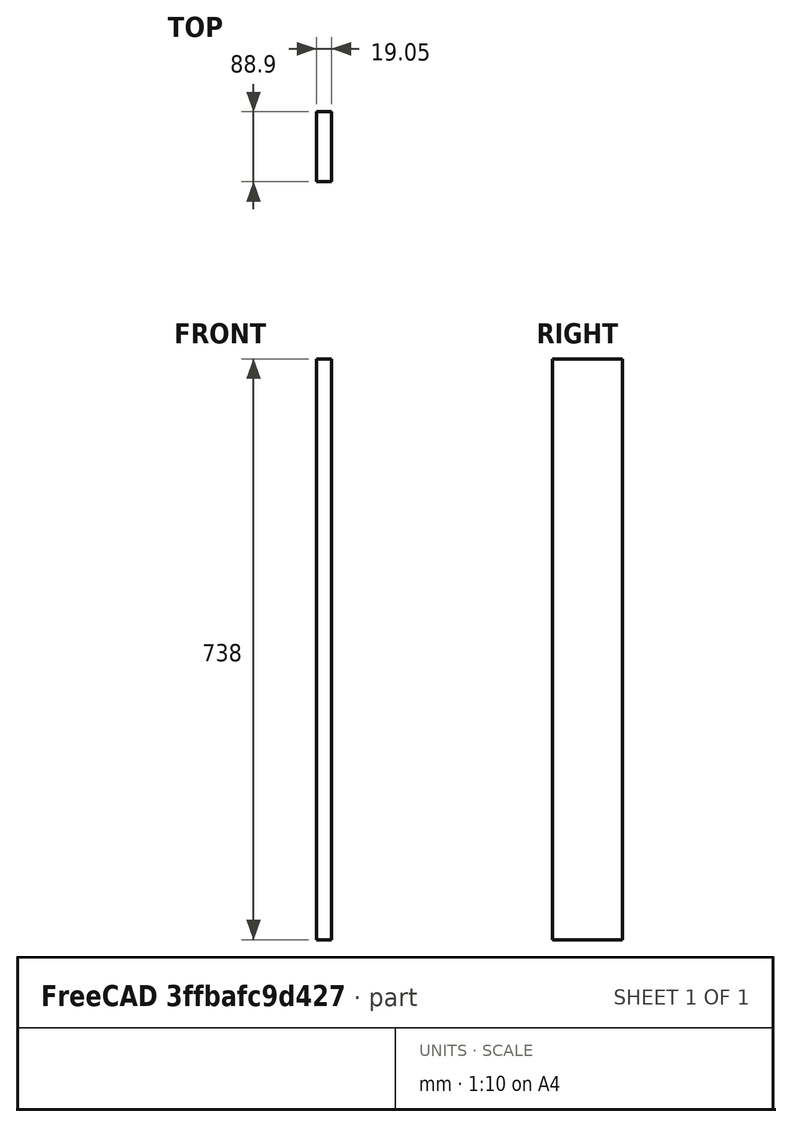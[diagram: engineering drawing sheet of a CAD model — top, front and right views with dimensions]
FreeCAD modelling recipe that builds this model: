
FCSTD DOCUMENT  (FreeCAD 0.19R24291 (Git))
Label: leg
License: All rights reserved
LicenseURL: http://en.wikipedia.org/wiki/All_rights_reserved
objects: Sketcher::SketchObject×1, PartDesign::Pad×1, PartDesign::Body×1
note: 4 computed .brp shape members not serialized (recipe doc carries the construction recipe); baked Part::Feature solids carry a one-line shape summary decoded from their .brp

FEATURE [Sketcher::SketchObject] Sketch
  FullyConstrained = true
  MapMode = 5
  Support = -> [XY_Plane]
  expr: Constraints[9] = 3.5 * 25.4
  expr: Constraints[10] = 3 / 4 * 25.4
  sketch-geometry (4):
    g0: LineSegment StartX=0 StartY=0 StartZ=0 EndX=19.05 EndY=0 EndZ=0
    g1: LineSegment StartX=19.05 StartY=0 StartZ=0 EndX=19.05 EndY=88.9 EndZ=0
    g2: LineSegment StartX=19.05 StartY=88.9 StartZ=0 EndX=0 EndY=88.9 EndZ=0
    g3: LineSegment StartX=0 StartY=88.9 StartZ=0 EndX=0 EndY=0 EndZ=0
  constraints (11):
    c: Coincident(g0,g1)
    c: Coincident(g1,g2)
    c: Coincident(g2,g3)
    c: Coincident(g3,g0)
    c: Horizontal(g0)
    c: Horizontal(g2)
    c: Vertical(g1)
    c: Vertical(g3)
    c: Coincident(g0,g-1)
    c: DistanceY(g3,g3) = 88.9
    c: DistanceX(g0,g0) = 19.05
FEATURE [PartDesign::Pad] Pad
  Direction = (1,1,1)
  Length = 738
  Length2 = 100
  Profile = -> Sketch
  Type = 0
  expr: Length = 738
FEATURE [PartDesign::Body] Body
  Group = -> [Sketch,Pad]
  Origin = -> Origin
  Tip = -> Pad
